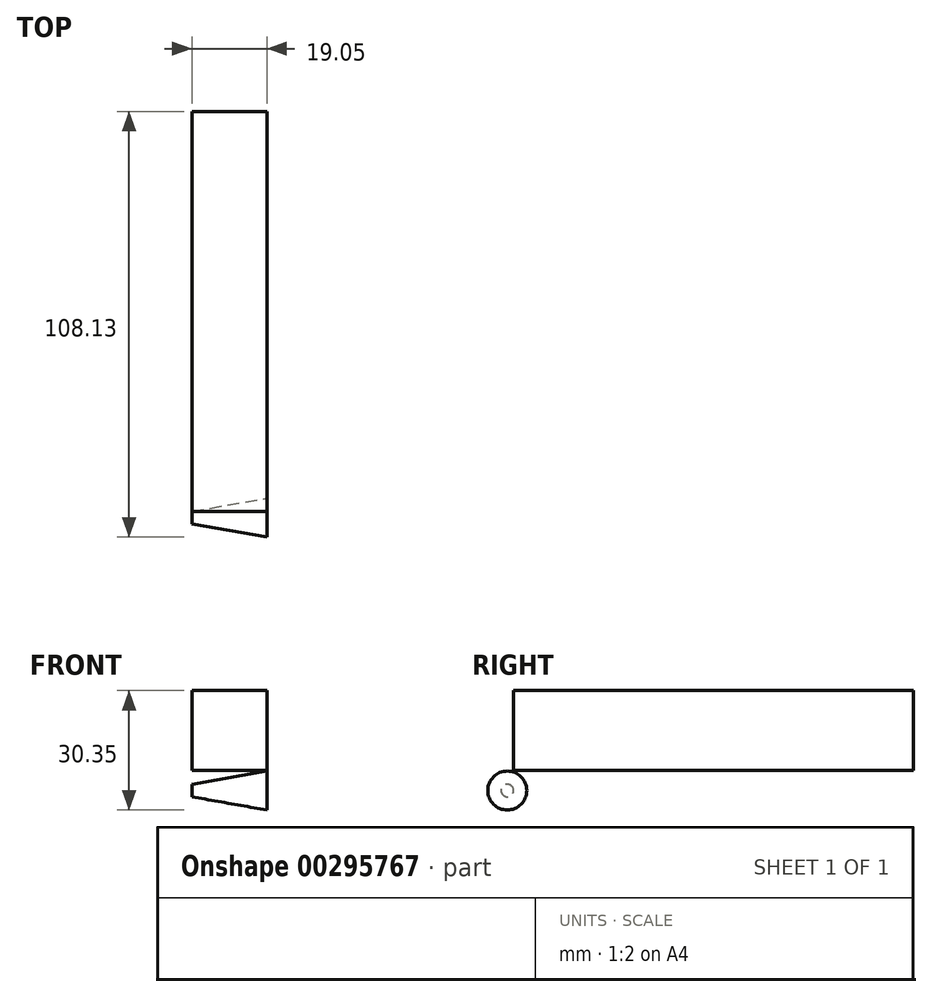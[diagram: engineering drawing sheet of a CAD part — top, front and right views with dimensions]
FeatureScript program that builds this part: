
annotation { "Feature Type Name" : "Feature", "Feature Type Description" : "" }
export const myFeature = defineFeature(function(context is Context, id is Id, definition is map)
    precondition{}
    {
        {
            var Q0;
            Q0=qCreatedBy(makeId("Right.planeOp"),FACE);
            var sketch = newSketch(context, id + "F0", { "sketchPlane" : qUnion([Q0])});
            skLineSegment(sketch, "E0.bottom", {"start": v(3.18, 3.18) * mm, "end": v(-3.17, 3.18) * mm});
            skLineSegment(sketch, "E0.top", {"start": v(3.18, 0) * mm, "end": v(-3.18, 0) * mm});
            skLineSegment(sketch, "E0.left", {"start": v(3.18, 3.18) * mm, "end": v(3.17, 0) * mm});
            skLineSegment(sketch, "E0.right", {"start": v(-3.17, 3.18) * mm, "end": v(-3.18, 0) * mm});
            skLineSegment(sketch, "E1.bottom", {"start": v(6.35, 5.16) * mm, "end": v(-6.35, 5.16) * mm});
            skLineSegment(sketch, "E1.top", {"start": v(6.35, 3.18) * mm, "end": v(3.18, 3.18) * mm});
            skLineSegment(sketch, "E1.left", {"start": v(6.35, 5.16) * mm, "end": v(6.35, 3.17) * mm});
            skLineSegment(sketch, "E1.right", {"start": v(-6.35, 5.16) * mm, "end": v(-6.35, 3.17) * mm});
            skCircle(sketch, "E2", {"center": v(0, 16.87) * mm, "radius": 6.35 * mm});
            skArc(sketch, "E3", {"start": v(-6.35, 5.16) * mm, "mid": v(-3.66, 8.5) * mm, "end": v(-4.75, 12.66) * mm});
            skArc(sketch, "E4", {"start": v(4.75, 12.66) * mm, "mid": v(3.66, 8.5) * mm, "end": v(6.35, 5.16) * mm});
            skLineSegment(sketch, "E5.trimOffspring", {"start": v(-3.17, 3.18) * mm, "end": v(-6.35, 3.18) * mm});
            skPoint(sketch, "E6", {"position": v(0, 4.17) * mm});
            skPoint(sketch, "E7", {"position": v(-6.35, 4.17) * mm});
            skPoint(sketch, "E8", {"position": v(6.35, 4.17) * mm});
            skLineSegment(sketch, "E9", {"start": v(-6.35, 5.16) * mm, "end": v(-4.86, 5.84) * mm, "construction": true});
            skCircle(sketch, "E10", {"center": v(0, 16.87) * mm, "radius": 3.97 * mm});
            skCircle(sketch, "E11", {"center": v(0, 16.87) * mm, "radius": 2.74 * mm, "construction": true});
            skCircle(sketch, "E12", {"center": v(0, 16.87) * mm, "radius": 3.4 * mm});
            skCircle(sketch, "E13", {"center": v(0, 16.87) * mm, "radius": 2.11 * mm});
            skPoint(sketch, "E14", {"position": v(0, 23.22) * mm});
            skSolve(sketch);
        }
        {
            var Q0;
            Q0=qCreatedBy(makeId("Right.planeOp"),FACE);
            var sketch = newSketch(context, id + "F1", { "sketchPlane" : qUnion([Q0])});
            skLineSegment(sketch, "E15.0.0", {"start": v(3.18, 3.18) * mm, "end": v(6.35, 3.18) * mm, "construction": true});
            skLineSegment(sketch, "E15.0.1", {"start": v(6.35, 3.17) * mm, "end": v(6.35, 5.16) * mm, "construction": true});
            skLineSegment(sketch, "E15.0.2", {"start": v(6.35, 5.16) * mm, "end": v(-6.35, 5.16) * mm, "construction": true});
            skLineSegment(sketch, "E15.0.3", {"start": v(-6.35, 5.16) * mm, "end": v(-6.35, 3.17) * mm, "construction": true});
            skLineSegment(sketch, "E15.0.4", {"start": v(-6.35, 3.18) * mm, "end": v(-3.17, 3.18) * mm, "construction": true});
            skLineSegment(sketch, "E15.0.5", {"start": v(-3.17, 3.18) * mm, "end": v(3.18, 3.18) * mm, "construction": true});
            skArc(sketch, "E16.0.0", {"start": v(6.35, 5.16) * mm, "mid": v(3.66, 8.5) * mm, "end": v(4.75, 12.66) * mm, "construction": true});
            skArc(sketch, "E16.0.1", {"start": v(4.75, 12.66) * mm, "mid": v(0, 10.52) * mm, "end": v(-4.75, 12.66) * mm, "construction": true});
            skArc(sketch, "E16.0.2", {"start": v(-4.75, 12.66) * mm, "mid": v(-3.66, 8.5) * mm, "end": v(-6.35, 5.16) * mm, "construction": true});
            skLineSegment(sketch, "E16.0.3", {"start": v(-6.35, 5.16) * mm, "end": v(6.35, 5.16) * mm, "construction": true});
            skArc(sketch, "E17.0.0", {"start": v(4.75, 12.66) * mm, "mid": v(0, 23.22) * mm, "end": v(-4.75, 12.66) * mm, "construction": true});
            skArc(sketch, "E17.0.1", {"start": v(-4.75, 12.66) * mm, "mid": v(0, 10.52) * mm, "end": v(4.75, 12.66) * mm, "construction": true});
            skLineSegment(sketch, "E18.bottom", {"start": v(-25.4, 3.18) * mm, "end": v(-101.6, 3.17) * mm});
            skLineSegment(sketch, "E18.top", {"start": v(-23.8, 12.66) * mm, "end": v(-101.6, 12.66) * mm});
            skLineSegment(sketch, "E18.right", {"start": v(-101.6, 3.17) * mm, "end": v(-101.6, 12.66) * mm});
            skPoint(sketch, "E19", {"position": v(-25.4, 5.16) * mm});
            skLineSegment(sketch, "E20", {"start": v(-25.4, 3.18) * mm, "end": v(-25.4, 5.16) * mm});
            skArc(sketch, "E21", {"start": v(-25.4, 5.16) * mm, "mid": v(-22.7, 8.5) * mm, "end": v(-23.8, 12.66) * mm});
            skPoint(sketch, "E22", {"position": v(6.35, 16.87) * mm});
            skPoint(sketch, "E23", {"position": v(-6.35, 16.87) * mm});
            skSolve(sketch);
        }
        {
            var Q0;
            Q0=qCreatedBy(makeId("Right.planeOp"),FACE);
            var sketch = newSketch(context, id + "F2", { "sketchPlane" : qUnion([Q0])});
            skArc(sketch, "E24.0", {"start": v(-6.35, 5.16) * mm, "mid": v(-3.66, 8.5) * mm, "end": v(-4.75, 12.66) * mm, "construction": true});
            skLineSegment(sketch, "E25.0", {"start": v(-6.35, 5.16) * mm, "end": v(-6.35, 3.17) * mm, "construction": true});
            skLineSegment(sketch, "E26.0", {"start": v(-3.17, 3.18) * mm, "end": v(-6.35, 3.18) * mm, "construction": true});
            skLineSegment(sketch, "E27.0", {"start": v(-3.17, 3.18) * mm, "end": v(-3.18, 0) * mm, "construction": true});
            skLineSegment(sketch, "E28.0", {"start": v(3.18, 0) * mm, "end": v(-3.18, 0) * mm, "construction": true});
            skLineSegment(sketch, "E29.0", {"start": v(3.18, 3.18) * mm, "end": v(3.17, 0) * mm});
            skLineSegment(sketch, "E30.0", {"start": v(6.35, 3.18) * mm, "end": v(3.18, 3.18) * mm});
            skLineSegment(sketch, "E31.0", {"start": v(6.35, 5.16) * mm, "end": v(6.35, 3.17) * mm});
            skArc(sketch, "E32.0", {"start": v(4.75, 12.66) * mm, "mid": v(3.66, 8.5) * mm, "end": v(6.35, 5.16) * mm});
            skPoint(sketch, "E33", {"position": v(0, 23.22) * mm});
            skArc(sketch, "E34", {"start": v(4.75, 12.66) * mm, "mid": v(5.77, 19.5) * mm, "end": v(-0.08, 23.22) * mm});
            skArc(sketch, "E35", {"start": v(-0.08, 23.22) * mm, "mid": v(-5.77, 14.23) * mm, "end": v(4.75, 12.66) * mm, "construction": true});
            skLineSegment(sketch, "E36", {"start": v(0, 23.22) * mm, "end": v(0, 25.4) * mm});
            skLineSegment(sketch, "E37", {"start": v(0, 25.4) * mm, "end": v(101.6, 25.4) * mm, "construction": true});
            skLineSegment(sketch, "E38", {"start": v(101.6, 25.4) * mm, "end": v(101.6, 5.16) * mm});
            skLineSegment(sketch, "E39", {"start": v(101.6, 0) * mm, "end": v(3.18, 0) * mm, "construction": true});
            skLineSegment(sketch, "E40", {"start": v(101.6, 5.16) * mm, "end": v(101.6, 0) * mm, "construction": true});
            skLineSegment(sketch, "E41", {"start": v(6.35, 5.16) * mm, "end": v(101.6, 5.16) * mm});
            skLineSegment(sketch, "E42", {"start": v(0, 25.4) * mm, "end": v(3.18, 25.4) * mm});
            skLineSegment(sketch, "E43", {"start": v(3.18, 25.4) * mm, "end": v(3.18, 28.58) * mm});
            skLineSegment(sketch, "E44", {"start": v(3.18, 28.58) * mm, "end": v(6.35, 28.58) * mm});
            skLineSegment(sketch, "E45", {"start": v(6.35, 28.58) * mm, "end": v(6.35, 30.56) * mm});
            skLineSegment(sketch, "E46", {"start": v(6.35, 30.56) * mm, "end": v(101.6, 30.56) * mm});
            skLineSegment(sketch, "E47", {"start": v(101.6, 30.56) * mm, "end": v(101.6, 25.4) * mm});
            skSolve(sketch);
        }
        {
            var Q0;
            Q0=qCreatedBy(makeId("Right.planeOp"),FACE);
            var sketch = newSketch(context, id + "F3", { "sketchPlane" : qUnion([Q0])});
            skPoint(sketch, "E48.0", {"position": v(0, 25.4) * mm});
            skPoint(sketch, "E49.0", {"position": v(101.6, 5.16) * mm});
            skLineSegment(sketch, "E50.bottom", {"start": v(0, 25.4) * mm, "end": v(101.6, 25.4) * mm});
            skLineSegment(sketch, "E50.top", {"start": v(0, 5.16) * mm, "end": v(101.6, 5.16) * mm});
            skLineSegment(sketch, "E50.left", {"start": v(0, 25.4) * mm, "end": v(0, 5.16) * mm});
            skLineSegment(sketch, "E50.right", {"start": v(101.6, 25.4) * mm, "end": v(101.6, 5.16) * mm});
            skSolve(sketch);
        }
        {
            var Q0;
            Q0 = qSketchRegion(id + "F3", true);
            extrude(context, id + "F4", {"entities" : qUnion([Q0]), "depth" : 19.05 * mm, "offsetDistance" : 25.4 * mm});
        }
        {
            var Q0;
            Q0=qCreatedBy(makeId("Top.planeOp"),FACE);
            var sketch = newSketch(context, id + "F5", { "sketchPlane" : qUnion([Q0])});
            skLineSegment(sketch, "E51.0", {"start": v(0, 0) * mm, "end": v(0, 101.6) * mm, "construction": true});
            skLineSegment(sketch, "E52.0", {"start": v(19.05, 0) * mm, "end": v(19.05, 101.6) * mm, "construction": true});
            skPoint(sketch, "E53.0", {"position": v(0, 0) * mm});
            skLineSegment(sketch, "E54", {"start": v(0, 0) * mm, "end": v(19.05, 3.36) * mm});
            skLineSegment(sketch, "E55", {"start": v(19.05, 3.36) * mm, "end": v(19.05, -1.59) * mm});
            skLineSegment(sketch, "E56", {"start": v(19.05, -1.59) * mm, "end": v(0, -1.59) * mm});
            skLineSegment(sketch, "E57", {"start": v(0, -1.59) * mm, "end": v(0, 0) * mm});
            skSolve(sketch);
        }
        {
            var Q0;
            Q0=makeQuery(id+"F5.imprint","IMPRINT",FACE,{"disambiguationData":[TD([[makeQuery(id+"F5.imprint","IMPRINT",EDGE,{"derivedFrom":sQuery(id+"F5.wireOp",EDGE,"E54")}),-1.0]])]});
            var Q1;
            Q1=sQuery(id+"F5.wireOp",EDGE,"E56");
            revolve(context, id + "F6", {"surfaceOperationType" : NewSurfaceOperationType.NEW, "entities" : qUnion([Q0]), "axis" : qUnion([Q1]), "revolveType" : RevolveType.FULL});
        }
    });
